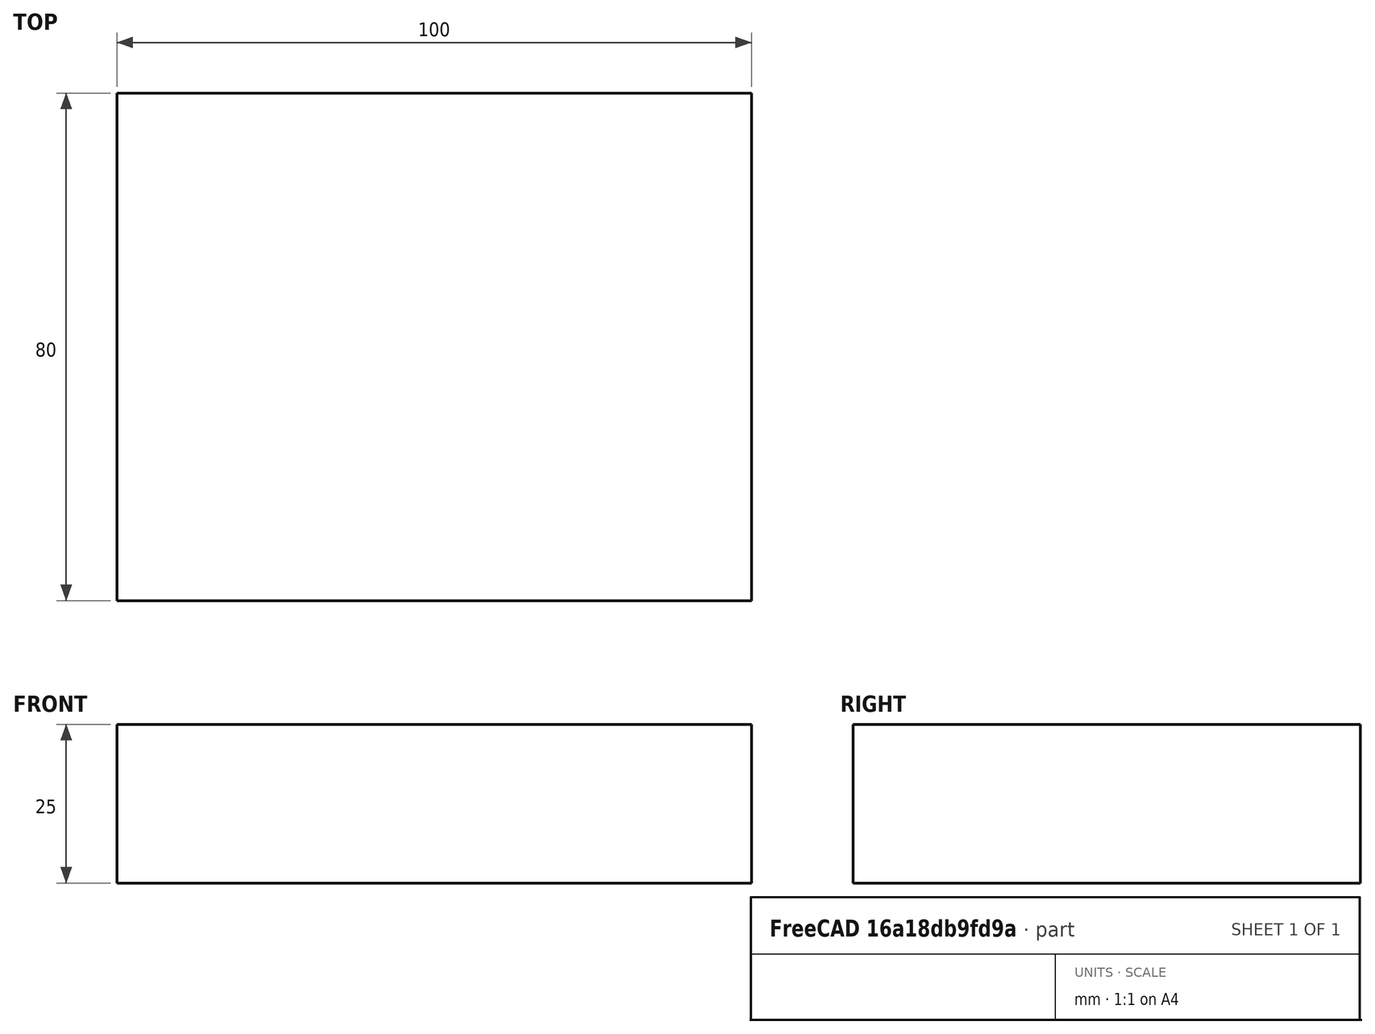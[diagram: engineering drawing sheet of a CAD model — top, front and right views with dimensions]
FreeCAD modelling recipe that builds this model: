
FCSTD DOCUMENT  (FreeCAD 0.18.4R)
Label: Case Bottom
License: All rights reserved
LicenseURL: http://en.wikipedia.org/wiki/All_rights_reserved
objects: Sketcher::SketchObject×1, PartDesign::Pad×1, PartDesign::Body×1
note: 4 computed .brp shape members not serialized (recipe doc carries the construction recipe); baked Part::Feature solids carry a one-line shape summary decoded from their .brp

FEATURE [Sketcher::SketchObject] Sketch
  MapMode = 5
  Support = -> [XY_Plane]
  sketch-geometry (4):
    g0: LineSegment StartX=-40 StartY=40 StartZ=0 EndX=60 EndY=40 EndZ=0
    g1: LineSegment StartX=60 StartY=40 StartZ=0 EndX=60 EndY=-40 EndZ=0
    g2: LineSegment StartX=60 StartY=-40 StartZ=0 EndX=-40 EndY=-40 EndZ=0
    g3: LineSegment StartX=-40 StartY=-40 StartZ=0 EndX=-40 EndY=40 EndZ=0
  constraints (11):
    c: Coincident(g0,g1)
    c: Coincident(g1,g2)
    c: Coincident(g2,g3)
    c: Coincident(g3,g0)
    c: Horizontal(g0)
    c: Horizontal(g2)
    c: Vertical(g1)
    c: DistanceX(g0,g0) = 100
    c: DistanceY(g1,g1) = 80
    c: Symmetric(g0,g2,g-1)
    c: DistanceX(g0,g-1) = 40
FEATURE [PartDesign::Pad] Pad
  Length = 25
  Length2 = 100
  Profile = -> Sketch
  Type = 0
FEATURE [PartDesign::Body] Body
  Group = -> [Sketch,Pad]
  Origin = -> Origin
  Tip = -> Pad
